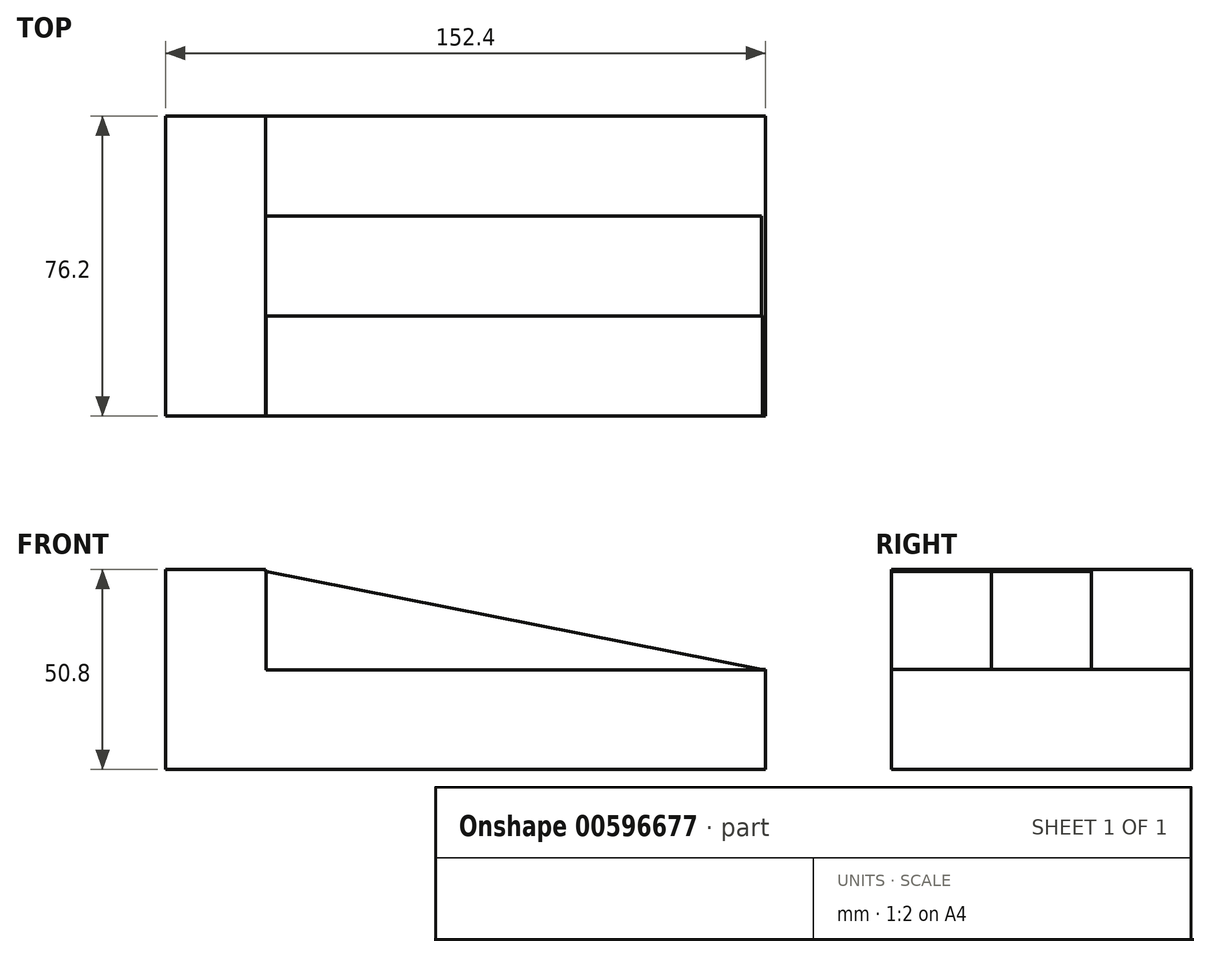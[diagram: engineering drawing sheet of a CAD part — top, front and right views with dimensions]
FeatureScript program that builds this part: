
annotation { "Feature Type Name" : "Feature", "Feature Type Description" : "" }
export const myFeature = defineFeature(function(context is Context, id is Id, definition is map)
    precondition{}
    {
        {
            var Q0;
            Q0=qCreatedBy(makeId("Front.planeOp"),FACE);
            var sketch = newSketch(context, id + "F0", { "sketchPlane" : qUnion([Q0])});
            skLineSegment(sketch, "E0", {"start": v(0, 0) * mm, "end": v(0, 50.8) * mm});
            skLineSegment(sketch, "E1", {"start": v(0, 50.8) * mm, "end": v(25.4, 50.8) * mm});
            skLineSegment(sketch, "E2", {"start": v(25.4, 50.8) * mm, "end": v(25.4, 25.4) * mm});
            skLineSegment(sketch, "E3", {"start": v(25.4, 25.4) * mm, "end": v(152.4, 25.4) * mm});
            skLineSegment(sketch, "E4", {"start": v(152.4, 25.4) * mm, "end": v(152.4, 0) * mm});
            skLineSegment(sketch, "E5", {"start": v(152.4, 0) * mm, "end": v(0, 0) * mm});
            skSolve(sketch);
        }
        {
            var Q0;
            Q0=makeQuery(id+"F0.imprint","IMPRINT",FACE,{"disambiguationData":[TD([[makeQuery(id+"F0.imprint","IMPRINT",EDGE,{"derivedFrom":sQuery(id+"F0.wireOp",EDGE,"E0")}),-1.0]])]});
            extrude(context, id + "F1", {"entities" : qUnion([Q0]), "oppositeDirection" : true, "depth" : 76.2 * mm, "offsetDistance" : 25.4 * mm});
        }
        {
            var Q0;
            Q0=qCreatedBy(makeId("Front.planeOp"),FACE);
            var sketch = newSketch(context, id + "F2", { "sketchPlane" : qUnion([Q0])});
            skLineSegment(sketch, "E6", {"start": v(25.02, 25.27) * mm, "end": v(25.02, 50.42) * mm});
            skLineSegment(sketch, "E7", {"start": v(25.02, 50.42) * mm, "end": v(152.02, 25.27) * mm});
            skLineSegment(sketch, "E8", {"start": v(152.02, 25.27) * mm, "end": v(25.02, 25.27) * mm});
            skSolve(sketch);
        }
        {
            var Q0;
            Q0=makeQuery(id+"F2.imprint","IMPRINT",FACE,{"disambiguationData":[TD([[makeQuery(id+"F2.imprint","IMPRINT",EDGE,{"derivedFrom":sQuery(id+"F2.wireOp",EDGE,"E6")}),-1.0]])]});
            extrude(context, id + "F3", {"entities" : qUnion([Q0]), "operationType" : NewBodyOperationType.ADD, "oppositeDirection" : true, "depth" : 50.8 * mm, "offsetDistance" : 25.4 * mm});
        }
        {
            var Q0;
            Q0=qCreatedBy(makeId("Front.planeOp"),FACE);
            var sketch = newSketch(context, id + "F4", { "sketchPlane" : qUnion([Q0])});
            skLineSegment(sketch, "E9", {"start": v(25.53, 51.18) * mm, "end": v(152.27, 25.27) * mm});
            skLineSegment(sketch, "E10", {"start": v(152.27, 25.27) * mm, "end": v(28.07, 25.27) * mm});
            skLineSegment(sketch, "E11", {"start": v(28.07, 25.27) * mm, "end": v(25.53, 25.27) * mm});
            skLineSegment(sketch, "E12", {"start": v(25.53, 25.27) * mm, "end": v(25.53, 51.18) * mm});
            skSolve(sketch);
        }
        {
            var Q0;
            Q0=makeQuery(id+"F4.imprint","IMPRINT",FACE,{"disambiguationData":[TD([[makeQuery(id+"F4.imprint","IMPRINT",EDGE,{"derivedFrom":sQuery(id+"F4.wireOp",EDGE,"E9")}),-1.0]])]});
            extrude(context, id + "F5", {"entities" : qUnion([Q0]), "operationType" : NewBodyOperationType.REMOVE, "oppositeDirection" : true, "depth" : 25.4 * mm, "offsetDistance" : 25.4 * mm});
        }
    });
